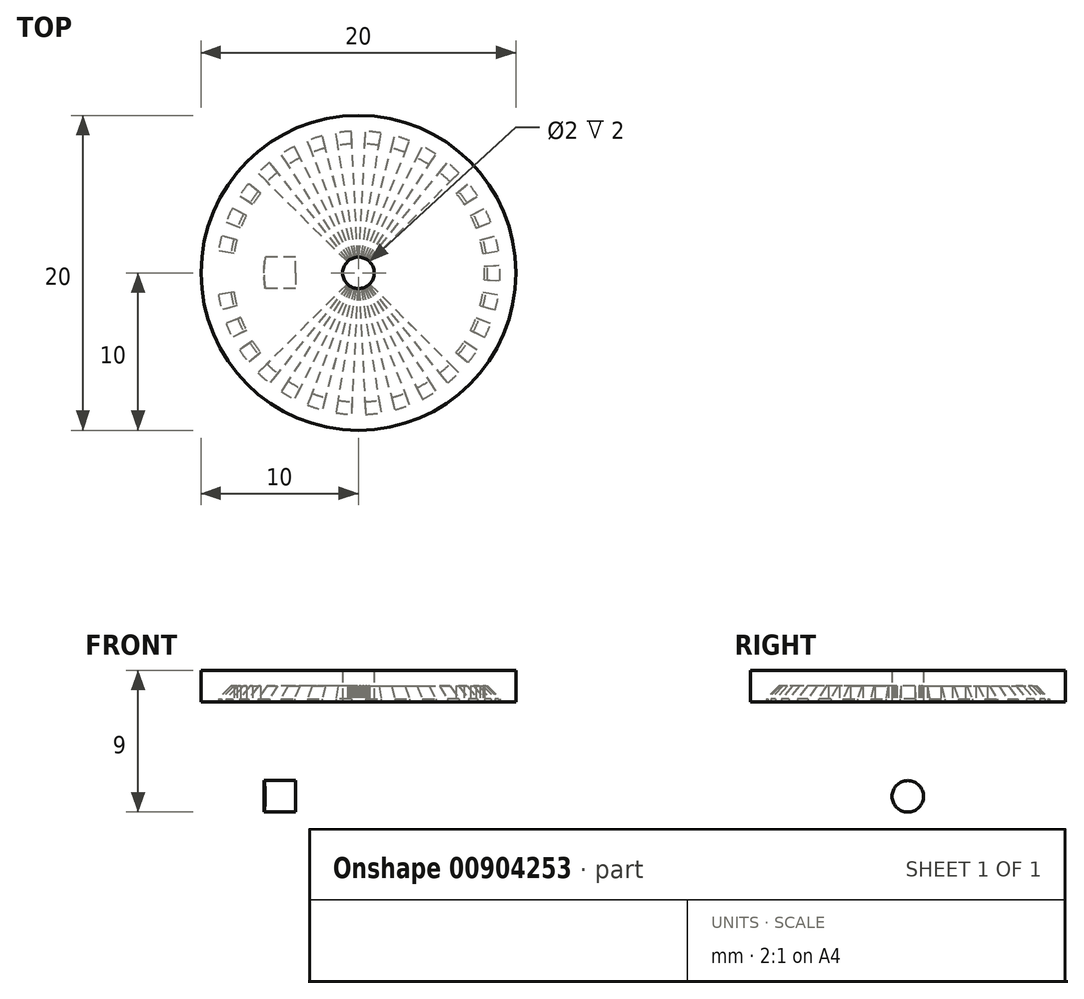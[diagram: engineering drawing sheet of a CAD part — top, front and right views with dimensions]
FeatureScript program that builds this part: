
annotation { "Feature Type Name" : "Feature", "Feature Type Description" : "" }
export const myFeature = defineFeature(function(context is Context, id is Id, definition is map)
    precondition{}
    {
        {
            var Q0;
            Q0=qCreatedBy(makeId("Front.planeOp"),FACE);
            var sketch = newSketch(context, id + "F0", { "sketchPlane" : qUnion([Q0])});
            skLineSegment(sketch, "E0.bottom", {"start": v(0, 0) * mm, "end": v(-5, 0) * mm});
            skLineSegment(sketch, "E0.top", {"start": v(0, 2) * mm, "end": v(-5, 2) * mm});
            skLineSegment(sketch, "E0.left", {"start": v(0, 0) * mm, "end": v(0, 2) * mm});
            skLineSegment(sketch, "E0.right", {"start": v(-5, 0) * mm, "end": v(-5, 2) * mm});
            skLineSegment(sketch, "E1.bottom", {"start": v(-5, 2) * mm, "end": v(-4, 2) * mm});
            skLineSegment(sketch, "E1.top", {"start": v(-5, 1) * mm, "end": v(-4, 1) * mm});
            skLineSegment(sketch, "E1.left", {"start": v(-5, 2) * mm, "end": v(-5, 1) * mm});
            skLineSegment(sketch, "E1.right", {"start": v(-4, 2) * mm, "end": v(-4, 1) * mm});
            skLineSegment(sketch, "E2.bottom", {"start": v(-4, 1) * mm, "end": v(-6, 1) * mm});
            skLineSegment(sketch, "E2.top", {"start": v(-4, 11) * mm, "end": v(-6, 11) * mm});
            skLineSegment(sketch, "E2.left", {"start": v(-4, 1) * mm, "end": v(-4, 11) * mm});
            skLineSegment(sketch, "E2.right", {"start": v(-6, 1) * mm, "end": v(-6, 11) * mm});
            skLineSegment(sketch, "E3", {"start": v(-1, 2) * mm, "end": v(-1, 0) * mm});
            skLineSegment(sketch, "E4.bottom", {"start": v(-6, 1) * mm, "end": v(-5, 1) * mm});
            skLineSegment(sketch, "E4.top", {"start": v(-6, 0) * mm, "end": v(-5, 0) * mm});
            skLineSegment(sketch, "E4.left", {"start": v(-6, 1) * mm, "end": v(-6, 0) * mm});
            skLineSegment(sketch, "E4.right", {"start": v(-5, 1) * mm, "end": v(-5, 0) * mm});
            skLineSegment(sketch, "E5.bottom", {"start": v(0, 0) * mm, "end": v(-6, 0) * mm});
            skLineSegment(sketch, "E5.top", {"start": v(0, -2) * mm, "end": v(-6, -2) * mm});
            skLineSegment(sketch, "E5.left", {"start": v(0, 0) * mm, "end": v(0, -2) * mm});
            skLineSegment(sketch, "E5.right", {"start": v(-6, 0) * mm, "end": v(-6, -2) * mm});
            skLineSegment(sketch, "E6.bottom", {"start": v(0, -2) * mm, "end": v(0, -2) * mm});
            skLineSegment(sketch, "E6.top", {"start": v(0, 0) * mm, "end": v(0, 0) * mm});
            skLineSegment(sketch, "E6.left", {"start": v(0, -2) * mm, "end": v(0, 0) * mm});
            skLineSegment(sketch, "E6.right", {"start": v(0, -2) * mm, "end": v(0, 0) * mm});
            skLineSegment(sketch, "E7.bottom", {"start": v(-6, -2) * mm, "end": v(-8, -2) * mm});
            skLineSegment(sketch, "E7.top", {"start": v(-6, 11) * mm, "end": v(-8, 11) * mm});
            skLineSegment(sketch, "E7.left", {"start": v(-6, -2) * mm, "end": v(-6, 11) * mm});
            skLineSegment(sketch, "E7.right", {"start": v(-8, -2) * mm, "end": v(-8, 11) * mm});
            skLineSegment(sketch, "E8.bottom", {"start": v(-4, 11) * mm, "end": v(-5, 11) * mm});
            skLineSegment(sketch, "E8.top", {"start": v(-4, 10) * mm, "end": v(-5, 10) * mm});
            skLineSegment(sketch, "E8.left", {"start": v(-4, 11) * mm, "end": v(-4, 10) * mm});
            skLineSegment(sketch, "E8.right", {"start": v(-5, 11) * mm, "end": v(-5, 10) * mm});
            skLineSegment(sketch, "E9.bottom", {"start": v(-5, 10) * mm, "end": v(0, 10) * mm});
            skLineSegment(sketch, "E9.top", {"start": v(-5, 12) * mm, "end": v(0, 12) * mm});
            skLineSegment(sketch, "E9.left", {"start": v(-5, 10) * mm, "end": v(-5, 12) * mm});
            skLineSegment(sketch, "E9.right", {"start": v(0, 10) * mm, "end": v(0, 12) * mm});
            skLineSegment(sketch, "E10.bottom", {"start": v(-8, 11) * mm, "end": v(-5, 11) * mm});
            skLineSegment(sketch, "E10.top", {"start": v(-8, 12) * mm, "end": v(-5, 12) * mm});
            skLineSegment(sketch, "E10.left", {"start": v(-8, 11) * mm, "end": v(-8, 12) * mm});
            skLineSegment(sketch, "E10.right", {"start": v(-5, 11) * mm, "end": v(-5, 12) * mm});
            skLineSegment(sketch, "E11", {"start": v(-6, 11) * mm, "end": v(-6, 12) * mm});
            skLineSegment(sketch, "E12.bottom", {"start": v(0, 12) * mm, "end": v(-8, 12) * mm});
            skLineSegment(sketch, "E12.top", {"start": v(0, 14) * mm, "end": v(-8, 14) * mm});
            skLineSegment(sketch, "E12.left", {"start": v(0, 12) * mm, "end": v(0, 14) * mm});
            skLineSegment(sketch, "E12.right", {"start": v(-8, 12) * mm, "end": v(-8, 14) * mm});
            skLineSegment(sketch, "E13", {"start": v(-1, 0) * mm, "end": v(-1, -2) * mm});
            skLineSegment(sketch, "E14", {"start": v(-1, -2) * mm, "end": v(-1, 14) * mm});
            skLineSegment(sketch, "E15.bottom", {"start": v(-8, 12) * mm, "end": v(-10, 12) * mm});
            skLineSegment(sketch, "E15.top", {"start": v(-8, 14) * mm, "end": v(-10, 14) * mm});
            skLineSegment(sketch, "E15.right", {"start": v(-10, 12) * mm, "end": v(-10, 14) * mm});
            skSolve(sketch);
        }
        {
            var Q0;
            {var subQ5=sQuery(id+"F0.wireOp",EDGE,"E7.bottom");Q0=makeQuery(id+"F0.imprint","IMPRINT",FACE,{"disambiguationData":[TD([[makeQuery(id+"F0.imprint","IMPRINT",EDGE,{"derivedFrom":subQ5}),-1.0]])]});}
            var Q1;
            {var subQ5=sQuery(id+"F0.wireOp",EDGE,"E5.bottom");var subQ7=makeQuery(id+"F0.imprint","INTERSECT",VERTEX,{"derivedFrom":[sQuery(id+"F0.wireOp",EDGE,"E4.right"),subQ5]});Q1=makeQuery(id+"F0.imprint","IMPRINT",FACE,{"disambiguationData":[TD([[makeQuery(id+"F0.imprint","IMPRINT",EDGE,{"disambiguationData":[TD([[subQ7,1.0]])],"derivedFrom":subQ5}),1.0]])]});}
            var Q2;
            {var subQ0=sQuery(id+"F0.wireOp",EDGE,"E12.right");Q2=makeQuery(id+"F0.imprint","IMPRINT",FACE,{"disambiguationData":[TD([[makeQuery(id+"F0.imprint","IMPRINT",EDGE,{"derivedFrom":subQ0}),-1.0]])]});}
            var Q3;
            Q3=makeQuery(id+"F0.imprint","IMPRINT",FACE,{"disambiguationData":[TD([[makeQuery(id+"F0.imprint","IMPRINT",EDGE,{"derivedFrom":sQuery(id+"F0.wireOp",EDGE,"E15.bottom")}),-1.0]])]});
            var Q4;
            {var subQ2=sQuery(id+"F0.wireOp",EDGE,"E10.left");Q4=makeQuery(id+"F0.imprint","IMPRINT",FACE,{"disambiguationData":[TD([[makeQuery(id+"F0.imprint","IMPRINT",EDGE,{"derivedFrom":subQ2}),-1.0]])]});}
            var Q5;
            Q5=sQuery(id+"F0.wireOp",EDGE,"E9.right");
            revolve(context, id + "F1", {"surfaceOperationType" : NewSurfaceOperationType.NEW, "entities" : qUnion([Q0, Q1, Q2, Q3, Q4]), "axis" : qUnion([Q5]), "revolveType" : RevolveType.FULL});
        }
        {
            var Q0;
            Q0=qCreatedBy(makeId("Front.planeOp"),FACE);
            var sketch = newSketch(context, id + "F2", { "sketchPlane" : qUnion([Q0])});
            skLineSegment(sketch, "E16.0", {"start": v(6, 0) * mm, "end": v(-6, 0) * mm});
            skLineSegment(sketch, "E17.0", {"start": v(10, 12) * mm, "end": v(-10, 12) * mm});
            skLineSegment(sketch, "E18", {"start": v(-6, 0) * mm, "end": v(-6, 12) * mm});
            skLineSegment(sketch, "E19", {"start": v(6, 0) * mm, "end": v(6, 12) * mm});
            skSolve(sketch);
        }
        {
            var Q0;
            Q0=makeQuery(id+"F2.imprint","IMPRINT",FACE,{"disambiguationData":[TD([[makeQuery(id+"F2.imprint","IMPRINT",EDGE,{"derivedFrom":sQuery(id+"F2.wireOp",EDGE,"E16.0")}),-1.0]])]});
            extrude(context, id + "F3", {"entities" : qUnion([Q0]), "operationType" : NewBodyOperationType.REMOVE, "oppositeDirection" : true, "depth" : 25 * mm, "offsetDistance" : 25 * mm});
        }
        {
            var Q0;
            Q0=makeQuery(id+"F2.imprint","IMPRINT",FACE,{"disambiguationData":[TD([[makeQuery(id+"F2.imprint","IMPRINT",EDGE,{"derivedFrom":sQuery(id+"F2.wireOp",EDGE,"E16.0")}),-1.0]])]});
            extrude(context, id + "F4", {"entities" : qUnion([Q0]), "operationType" : NewBodyOperationType.REMOVE, "oppositeDirection" : true, "depth" : -25 * mm, "offsetDistance" : 25 * mm});
        }
        {
            var Q0;
            Q0=makeQuery(id+"F1.opRevolve","SWEPT_FACE",FACE,{"disambiguationData":[OSD([sQuery(id+"F0.wireOp",EDGE,"E12.top"),sQuery(id+"F0.wireOp",EDGE,"E15.top")])]});
            var sketch = newSketch(context, id + "F5", { "sketchPlane" : qUnion([Q0])});
            skLineSegment(sketch, "E20", {"start": v(-0.5, 9.99) * mm, "end": v(0.5, 9.99) * mm});
            skLineSegment(sketch, "E21", {"start": v(0, 0) * mm, "end": v(0.5, 9.99) * mm});
            skLineSegment(sketch, "E22", {"start": v(0, 0) * mm, "end": v(-0.5, 9.99) * mm});
            skCircle(sketch, "E23", {"center": v(0, 0) * mm, "radius": 9 * mm});
            skLineSegment(sketch, "E24", {"start": v(0, 0) * mm, "end": v(9, 0) * mm});
            skLineSegment(sketch, "E25", {"start": v(9, 0) * mm, "end": v(10, 0) * mm});
            skLineSegment(sketch, "E26.1.0", {"start": v(0, 0) * mm, "end": v(-2.57, 9.67) * mm});
            skLineSegment(sketch, "E26.1.1", {"start": v(0, 0) * mm, "end": v(-1.59, 9.87) * mm});
            skLineSegment(sketch, "E26.2.0", {"start": v(0, 0) * mm, "end": v(-4.52, 8.92) * mm});
            skLineSegment(sketch, "E26.2.1", {"start": v(0, 0) * mm, "end": v(-3.6, 9.33) * mm});
            skLineSegment(sketch, "E27.2.3.0", {"start": v(0, 0) * mm, "end": v(-6.28, 7.79) * mm});
            skLineSegment(sketch, "E27.3.3.0", {"start": v(0, 0) * mm, "end": v(-5.47, 8.37) * mm});
            skLineSegment(sketch, "E27.2.4.0", {"start": v(0, 0) * mm, "end": v(-7.76, 6.31) * mm});
            skLineSegment(sketch, "E27.3.4.0", {"start": v(0, 0) * mm, "end": v(-7.09, 7.05) * mm});
            skLineSegment(sketch, "E27.2.5.0", {"start": v(0, 0) * mm, "end": v(-8.9, 4.56) * mm});
            skLineSegment(sketch, "E27.3.5.0", {"start": v(0, 0) * mm, "end": v(-8.4, 5.43) * mm});
            skLineSegment(sketch, "E27.2.6.0", {"start": v(0, 0) * mm, "end": v(-9.65, 2.61) * mm});
            skLineSegment(sketch, "E27.3.6.0", {"start": v(0, 0) * mm, "end": v(-9.34, 3.56) * mm});
            skLineSegment(sketch, "E27.2.7.0", {"start": v(0, 0) * mm, "end": v(-9.99, 0.55) * mm});
            skLineSegment(sketch, "E27.3.7.0", {"start": v(0, 0) * mm, "end": v(-9.88, 1.54) * mm});
            skLineSegment(sketch, "E27.2.8.0", {"start": v(0, 0) * mm, "end": v(-9.88, -1.54) * mm});
            skLineSegment(sketch, "E27.3.8.0", {"start": v(0, 0) * mm, "end": v(-9.99, -0.55) * mm});
            skLineSegment(sketch, "E27.2.9.0", {"start": v(0, 0) * mm, "end": v(-9.34, -3.56) * mm});
            skLineSegment(sketch, "E27.3.9.0", {"start": v(0, 0) * mm, "end": v(-9.65, -2.61) * mm});
            skLineSegment(sketch, "E27.2.10.0", {"start": v(0, 0) * mm, "end": v(-8.4, -5.43) * mm});
            skLineSegment(sketch, "E27.3.10.0", {"start": v(0, 0) * mm, "end": v(-8.9, -4.56) * mm});
            skLineSegment(sketch, "E27.2.11.0", {"start": v(0, 0) * mm, "end": v(-7.09, -7.05) * mm});
            skLineSegment(sketch, "E27.3.11.0", {"start": v(0, 0) * mm, "end": v(-7.76, -6.31) * mm});
            skLineSegment(sketch, "E27.2.12.0", {"start": v(0, 0) * mm, "end": v(-5.47, -8.37) * mm});
            skLineSegment(sketch, "E27.3.12.0", {"start": v(0, 0) * mm, "end": v(-6.28, -7.79) * mm});
            skLineSegment(sketch, "E27.2.13.0", {"start": v(0, 0) * mm, "end": v(-3.6, -9.33) * mm});
            skLineSegment(sketch, "E27.3.13.0", {"start": v(0, 0) * mm, "end": v(-4.52, -8.92) * mm});
            skLineSegment(sketch, "E27.2.14.0", {"start": v(0, 0) * mm, "end": v(-1.59, -9.87) * mm});
            skLineSegment(sketch, "E27.3.14.0", {"start": v(0, 0) * mm, "end": v(-2.57, -9.67) * mm});
            skLineSegment(sketch, "E27.2.15.0", {"start": v(0, 0) * mm, "end": v(0.5, -9.99) * mm});
            skLineSegment(sketch, "E27.3.15.0", {"start": v(0, 0) * mm, "end": v(-0.5, -9.99) * mm});
            skLineSegment(sketch, "E27.2.16.0", {"start": v(0, 0) * mm, "end": v(2.57, -9.67) * mm});
            skLineSegment(sketch, "E27.3.16.0", {"start": v(0, 0) * mm, "end": v(1.59, -9.87) * mm});
            skLineSegment(sketch, "E27.2.17.0", {"start": v(0, 0) * mm, "end": v(4.52, -8.92) * mm});
            skLineSegment(sketch, "E27.3.17.0", {"start": v(0, 0) * mm, "end": v(3.6, -9.33) * mm});
            skLineSegment(sketch, "E27.2.18.0", {"start": v(0, 0) * mm, "end": v(6.28, -7.79) * mm});
            skLineSegment(sketch, "E27.3.18.0", {"start": v(0, 0) * mm, "end": v(5.47, -8.37) * mm});
            skLineSegment(sketch, "E27.2.19.0", {"start": v(0, 0) * mm, "end": v(7.76, -6.31) * mm});
            skLineSegment(sketch, "E27.3.19.0", {"start": v(0, 0) * mm, "end": v(7.09, -7.05) * mm});
            skLineSegment(sketch, "E27.2.20.0", {"start": v(0, 0) * mm, "end": v(8.9, -4.56) * mm});
            skLineSegment(sketch, "E27.3.20.0", {"start": v(0, 0) * mm, "end": v(8.4, -5.43) * mm});
            skLineSegment(sketch, "E27.2.21.0", {"start": v(0, 0) * mm, "end": v(9.65, -2.61) * mm});
            skLineSegment(sketch, "E27.3.21.0", {"start": v(0, 0) * mm, "end": v(9.34, -3.56) * mm});
            skLineSegment(sketch, "E27.2.22.0", {"start": v(0, 0) * mm, "end": v(9.99, -0.55) * mm});
            skLineSegment(sketch, "E27.3.22.0", {"start": v(0, 0) * mm, "end": v(9.88, -1.54) * mm});
            skLineSegment(sketch, "E27.2.23.0", {"start": v(0, 0) * mm, "end": v(9.88, 1.54) * mm});
            skLineSegment(sketch, "E27.3.23.0", {"start": v(0, 0) * mm, "end": v(9.99, 0.55) * mm});
            skLineSegment(sketch, "E27.2.24.0", {"start": v(0, 0) * mm, "end": v(9.34, 3.56) * mm});
            skLineSegment(sketch, "E27.3.24.0", {"start": v(0, 0) * mm, "end": v(9.65, 2.61) * mm});
            skLineSegment(sketch, "E28.2.25.0", {"start": v(0, 0) * mm, "end": v(8.4, 5.43) * mm});
            skLineSegment(sketch, "E28.3.25.0", {"start": v(0, 0) * mm, "end": v(8.9, 4.56) * mm});
            skLineSegment(sketch, "E29.2.26.0", {"start": v(0, 0) * mm, "end": v(7.09, 7.05) * mm});
            skLineSegment(sketch, "E29.3.26.0", {"start": v(0, 0) * mm, "end": v(7.76, 6.31) * mm});
            skLineSegment(sketch, "E29.2.27.0", {"start": v(0, 0) * mm, "end": v(5.47, 8.37) * mm});
            skLineSegment(sketch, "E29.3.27.0", {"start": v(0, 0) * mm, "end": v(6.28, 7.79) * mm});
            skLineSegment(sketch, "E29.2.28.0", {"start": v(0, 0) * mm, "end": v(3.6, 9.33) * mm});
            skLineSegment(sketch, "E29.3.28.0", {"start": v(0, 0) * mm, "end": v(4.52, 8.92) * mm});
            skLineSegment(sketch, "E29.2.29.0", {"start": v(0, 0) * mm, "end": v(1.59, 9.87) * mm});
            skLineSegment(sketch, "E29.3.29.0", {"start": v(0, 0) * mm, "end": v(2.57, 9.67) * mm});
            skSolve(sketch);
        }
        {
            var Q0;
            {var subQ0=sQuery(id+"F2.wireOp",EDGE,"E18");Q0=makeQuery(id+"F4.boolean.opBoolean","MERGE",FACE,{"derivedFrom":[makeQuery(id+"F3.boolean.opBoolean","COPY",FACE,{"derivedFrom":makeQuery(id+"F3.opExtrude","SWEPT_FACE",FACE,{"disambiguationData":[OSD([subQ0])]})})],"fromTools":[makeQuery(id+"F4.opExtrude","SWEPT_FACE",FACE,{"disambiguationData":[OSD([subQ0])]})]});}
            var sketch = newSketch(context, id + "F6", { "sketchPlane" : qUnion([Q0])});
            skLineSegment(sketch, "E30.0", {"start": v(10, 12) * mm, "end": v(-10, 12) * mm});
            skLineSegment(sketch, "E31.0", {"start": v(5.3, 0) * mm, "end": v(8, 0) * mm});
            skLineSegment(sketch, "E32.0", {"start": v(-5.3, 0) * mm, "end": v(-8, 0) * mm});
            skLineSegment(sketch, "E33", {"start": v(-5.3, 0) * mm, "end": v(5.3, 0) * mm});
            skLineSegment(sketch, "E34", {"start": v(0, 0) * mm, "end": v(0, 12) * mm});
            skLineSegment(sketch, "E35.0", {"start": v(-5.3, 12) * mm, "end": v(-5.3, 0) * mm});
            skLineSegment(sketch, "E36.0", {"start": v(5.3, 12) * mm, "end": v(5.3, 0) * mm});
            skLineSegment(sketch, "E37", {"start": v(-5.3, 6) * mm, "end": v(5.3, 6) * mm});
            skCircle(sketch, "E38", {"center": v(0, 6) * mm, "radius": 1 * mm});
            skSolve(sketch);
        }
        {
            var Q0;
            {var subQ0=sQuery(id+"F6.wireOp",EDGE,"E37");var subQ1=sQuery(id+"F6.wireOp",EDGE,"E34");var subQ2=makeQuery(id+"F6.imprint","INTERSECT",VERTEX,{"derivedFrom":[subQ1,subQ0]});Q0=makeQuery(id+"F6.imprint","IMPRINT",FACE,{"disambiguationData":[TD([[makeQuery(id+"F6.imprint","IMPRINT",EDGE,{"disambiguationData":[TD([[subQ2,-1.0]])],"derivedFrom":subQ1}),-1.0]])]});}
            var Q1;
            {var subQ0=sQuery(id+"F6.wireOp",EDGE,"E38");var subQ1=sQuery(id+"F6.wireOp",EDGE,"E34");var subQ2=makeQuery(id+"F6.imprint","INTERSECT",VERTEX,{"disambiguationData":[OD(0.0)],"derivedFrom":[subQ1,subQ0]});Q1=makeQuery(id+"F6.imprint","IMPRINT",FACE,{"disambiguationData":[TD([[makeQuery(id+"F6.imprint","IMPRINT",EDGE,{"disambiguationData":[TD([[subQ2,-1.0]])],"derivedFrom":subQ1}),-1.0]])]});}
            var Q2;
            {var subQ0=sQuery(id+"F6.wireOp",EDGE,"E38");var subQ1=sQuery(id+"F6.wireOp",EDGE,"E34");var subQ2=makeQuery(id+"F6.imprint","INTERSECT",VERTEX,{"disambiguationData":[OD(0.0)],"derivedFrom":[subQ1,subQ0]});Q2=makeQuery(id+"F6.imprint","IMPRINT",FACE,{"disambiguationData":[TD([[makeQuery(id+"F6.imprint","IMPRINT",EDGE,{"disambiguationData":[TD([[subQ2,-1.0]])],"derivedFrom":subQ1}),1.0]])]});}
            var Q3;
            {var subQ0=sQuery(id+"F6.wireOp",EDGE,"E37");var subQ1=sQuery(id+"F6.wireOp",EDGE,"E34");var subQ2=makeQuery(id+"F6.imprint","INTERSECT",VERTEX,{"derivedFrom":[subQ1,subQ0]});Q3=makeQuery(id+"F6.imprint","IMPRINT",FACE,{"disambiguationData":[TD([[makeQuery(id+"F6.imprint","IMPRINT",EDGE,{"disambiguationData":[TD([[subQ2,-1.0]])],"derivedFrom":subQ1}),1.0]])]});}
            extrude(context, id + "F7", {"entities" : qUnion([Q0, Q1, Q2, Q3]), "operationType" : NewBodyOperationType.ADD, "depth" : 2 * mm, "offsetDistance" : 25 * mm});
        }
        {
            var Q0;
            {var subQ0=sQuery(id+"F2.wireOp",EDGE,"E17.0");Q0=makeQuery(id+"F4.boolean.opBoolean","MERGE",FACE,{"derivedFrom":[makeQuery(id+"F3.boolean.opBoolean","MERGE",FACE,{"derivedFrom":[makeQuery(id+"F1.opRevolve","SWEPT_FACE",FACE,{"disambiguationData":[OSD([sQuery(id+"F0.wireOp",EDGE,"E12.bottom")])]}),makeQuery(id+"F1.opRevolve","SWEPT_FACE",FACE,{"disambiguationData":[OSD([sQuery(id+"F0.wireOp",EDGE,"E15.bottom")])]})],"fromTools":[makeQuery(id+"F3.opExtrude","SWEPT_FACE",FACE,{"disambiguationData":[OSD([subQ0])]})]})],"fromTools":[makeQuery(id+"F4.opExtrude","SWEPT_FACE",FACE,{"disambiguationData":[OSD([subQ0])]})]});}
            var sketch = newSketch(context, id + "F8", { "sketchPlane" : qUnion([Q0])});
            skCircle(sketch, "E39.0", {"center": v(0, 0) * mm, "radius": 9 * mm});
            skLineSegment(sketch, "E40.0", {"start": v(0, 0) * mm, "end": v(-7.76, 6.31) * mm});
            skLineSegment(sketch, "E41.0", {"start": v(0, 0) * mm, "end": v(-7.09, 7.05) * mm});
            skLineSegment(sketch, "E42.0", {"start": v(0, 0) * mm, "end": v(-6.28, 7.79) * mm});
            skLineSegment(sketch, "E43.0", {"start": v(0, 0) * mm, "end": v(-5.47, 8.37) * mm});
            skLineSegment(sketch, "E44.0", {"start": v(0, 0) * mm, "end": v(-4.52, 8.92) * mm});
            skLineSegment(sketch, "E45.0", {"start": v(0, 0) * mm, "end": v(-3.6, 9.33) * mm});
            skLineSegment(sketch, "E46.0", {"start": v(0, 0) * mm, "end": v(-2.57, 9.67) * mm});
            skLineSegment(sketch, "E47.0", {"start": v(0, 0) * mm, "end": v(-1.59, 9.87) * mm});
            skLineSegment(sketch, "E48.0", {"start": v(0, 0) * mm, "end": v(-0.5, 9.99) * mm});
            skLineSegment(sketch, "E49.0", {"start": v(0, 0) * mm, "end": v(0.5, 9.99) * mm});
            skLineSegment(sketch, "E50.0", {"start": v(0, 0) * mm, "end": v(1.59, 9.87) * mm});
            skLineSegment(sketch, "E51.0", {"start": v(0, 0) * mm, "end": v(2.57, 9.67) * mm});
            skLineSegment(sketch, "E52.0", {"start": v(0, 0) * mm, "end": v(3.6, 9.33) * mm});
            skLineSegment(sketch, "E53.0", {"start": v(0, 0) * mm, "end": v(4.52, 8.92) * mm});
            skLineSegment(sketch, "E54.0", {"start": v(0, 0) * mm, "end": v(5.47, 8.37) * mm});
            skLineSegment(sketch, "E55.0", {"start": v(0, 0) * mm, "end": v(6.28, 7.79) * mm});
            skLineSegment(sketch, "E56.0", {"start": v(0, 0) * mm, "end": v(7.09, 7.05) * mm});
            skLineSegment(sketch, "E57.0", {"start": v(0, 0) * mm, "end": v(7.76, 6.31) * mm});
            skLineSegment(sketch, "E58.0", {"start": v(0, 0) * mm, "end": v(8.4, 5.43) * mm});
            skLineSegment(sketch, "E59.0", {"start": v(0, 0) * mm, "end": v(8.9, 4.56) * mm});
            skLineSegment(sketch, "E60.0", {"start": v(0, 0) * mm, "end": v(9.34, 3.56) * mm});
            skLineSegment(sketch, "E61.0", {"start": v(0, 0) * mm, "end": v(9.65, 2.61) * mm});
            skLineSegment(sketch, "E62.0", {"start": v(0, 0) * mm, "end": v(9.88, 1.54) * mm});
            skLineSegment(sketch, "E63.0", {"start": v(0, 0) * mm, "end": v(9.99, 0.55) * mm});
            skLineSegment(sketch, "E64.0", {"start": v(0, 0) * mm, "end": v(9.99, -0.55) * mm});
            skLineSegment(sketch, "E65.0", {"start": v(0, 0) * mm, "end": v(9.88, -1.54) * mm});
            skLineSegment(sketch, "E66.0", {"start": v(0, 0) * mm, "end": v(9.65, -2.61) * mm});
            skLineSegment(sketch, "E67.0", {"start": v(0, 0) * mm, "end": v(9.34, -3.56) * mm});
            skLineSegment(sketch, "E68.0", {"start": v(0, 0) * mm, "end": v(8.9, -4.56) * mm});
            skLineSegment(sketch, "E69.0", {"start": v(0, 0) * mm, "end": v(8.4, -5.43) * mm});
            skLineSegment(sketch, "E70.0", {"start": v(0, 0) * mm, "end": v(7.76, -6.31) * mm});
            skLineSegment(sketch, "E71.0", {"start": v(0, 0) * mm, "end": v(7.09, -7.05) * mm});
            skLineSegment(sketch, "E72.0", {"start": v(0, 0) * mm, "end": v(6.28, -7.79) * mm});
            skLineSegment(sketch, "E73.0", {"start": v(0, 0) * mm, "end": v(5.47, -8.37) * mm});
            skLineSegment(sketch, "E74.0", {"start": v(0, 0) * mm, "end": v(4.52, -8.92) * mm});
            skLineSegment(sketch, "E75.0", {"start": v(0, 0) * mm, "end": v(3.6, -9.33) * mm});
            skLineSegment(sketch, "E76.0", {"start": v(0, 0) * mm, "end": v(2.57, -9.67) * mm});
            skLineSegment(sketch, "E77.0", {"start": v(0, 0) * mm, "end": v(1.59, -9.87) * mm});
            skLineSegment(sketch, "E78.0", {"start": v(0, 0) * mm, "end": v(0.5, -9.99) * mm});
            skLineSegment(sketch, "E79.0", {"start": v(0, 0) * mm, "end": v(-0.5, -9.99) * mm});
            skLineSegment(sketch, "E80.0", {"start": v(0, 0) * mm, "end": v(-1.59, -9.87) * mm});
            skLineSegment(sketch, "E81.0", {"start": v(0, 0) * mm, "end": v(-2.57, -9.67) * mm});
            skLineSegment(sketch, "E82.0", {"start": v(0, 0) * mm, "end": v(-3.6, -9.33) * mm});
            skLineSegment(sketch, "E83.0", {"start": v(0, 0) * mm, "end": v(-4.52, -8.92) * mm});
            skLineSegment(sketch, "E84.0", {"start": v(0, 0) * mm, "end": v(-5.47, -8.37) * mm});
            skLineSegment(sketch, "E85.0", {"start": v(0, 0) * mm, "end": v(-6.28, -7.79) * mm});
            skLineSegment(sketch, "E86.0", {"start": v(0, 0) * mm, "end": v(-7.09, -7.05) * mm});
            skLineSegment(sketch, "E87.0", {"start": v(0, 0) * mm, "end": v(-7.76, -6.31) * mm});
            skLineSegment(sketch, "E88.0", {"start": v(0, 0) * mm, "end": v(-8.4, -5.43) * mm});
            skLineSegment(sketch, "E89.0", {"start": v(0, 0) * mm, "end": v(-8.9, -4.56) * mm});
            skLineSegment(sketch, "E90.0", {"start": v(0, 0) * mm, "end": v(-9.34, -3.56) * mm});
            skLineSegment(sketch, "E91.0", {"start": v(0, 0) * mm, "end": v(-9.65, -2.61) * mm});
            skLineSegment(sketch, "E92.0", {"start": v(0, 0) * mm, "end": v(-9.88, -1.54) * mm});
            skLineSegment(sketch, "E93.0", {"start": v(0, 0) * mm, "end": v(-9.99, -0.55) * mm});
            skLineSegment(sketch, "E94.0", {"start": v(0, 0) * mm, "end": v(-9.99, 0.55) * mm});
            skLineSegment(sketch, "E95.0", {"start": v(0, 0) * mm, "end": v(-9.88, 1.54) * mm});
            skLineSegment(sketch, "E96.0", {"start": v(0, 0) * mm, "end": v(-9.65, 2.61) * mm});
            skLineSegment(sketch, "E97.0", {"start": v(0, 0) * mm, "end": v(-9.34, 3.56) * mm});
            skLineSegment(sketch, "E98.0", {"start": v(0, 0) * mm, "end": v(-8.9, 4.56) * mm});
            skLineSegment(sketch, "E99.0", {"start": v(0, 0) * mm, "end": v(-8.4, 5.43) * mm});
            skSolve(sketch);
        }
        {
            var Q0;
            {var subQ0=sQuery(id+"F8.wireOp",EDGE,"E48.0");var subQ1=sQuery(id+"F8.wireOp",EDGE,"E39.0");var subQ2=makeQuery(id+"F8.imprint","INTERSECT",VERTEX,{"derivedFrom":[subQ1,subQ0]});Q0=makeQuery(id+"F8.imprint","IMPRINT",FACE,{"disambiguationData":[TD([[makeQuery(id+"F8.imprint","IMPRINT",EDGE,{"disambiguationData":[TD([[subQ2,-1.0]])],"derivedFrom":subQ1}),1.0]])]});}
            var Q1;
            {var subQ0=sQuery(id+"F8.wireOp",EDGE,"E50.0");var subQ1=sQuery(id+"F8.wireOp",EDGE,"E39.0");var subQ2=makeQuery(id+"F8.imprint","INTERSECT",VERTEX,{"derivedFrom":[subQ1,subQ0]});Q1=makeQuery(id+"F8.imprint","IMPRINT",FACE,{"disambiguationData":[TD([[makeQuery(id+"F8.imprint","IMPRINT",EDGE,{"disambiguationData":[TD([[subQ2,-1.0]])],"derivedFrom":subQ1}),1.0]])]});}
            var Q2;
            {var subQ0=sQuery(id+"F8.wireOp",EDGE,"E52.0");var subQ1=sQuery(id+"F8.wireOp",EDGE,"E39.0");var subQ2=makeQuery(id+"F8.imprint","INTERSECT",VERTEX,{"derivedFrom":[subQ1,subQ0]});Q2=makeQuery(id+"F8.imprint","IMPRINT",FACE,{"disambiguationData":[TD([[makeQuery(id+"F8.imprint","IMPRINT",EDGE,{"disambiguationData":[TD([[subQ2,-1.0]])],"derivedFrom":subQ1}),1.0]])]});}
            var Q3;
            {var subQ0=sQuery(id+"F8.wireOp",EDGE,"E54.0");var subQ1=sQuery(id+"F8.wireOp",EDGE,"E39.0");var subQ2=makeQuery(id+"F8.imprint","INTERSECT",VERTEX,{"derivedFrom":[subQ1,subQ0]});Q3=makeQuery(id+"F8.imprint","IMPRINT",FACE,{"disambiguationData":[TD([[makeQuery(id+"F8.imprint","IMPRINT",EDGE,{"disambiguationData":[TD([[subQ2,-1.0]])],"derivedFrom":subQ1}),1.0]])]});}
            var Q4;
            {var subQ0=sQuery(id+"F8.wireOp",EDGE,"E56.0");var subQ1=sQuery(id+"F8.wireOp",EDGE,"E39.0");var subQ2=makeQuery(id+"F8.imprint","INTERSECT",VERTEX,{"derivedFrom":[subQ1,subQ0]});Q4=makeQuery(id+"F8.imprint","IMPRINT",FACE,{"disambiguationData":[TD([[makeQuery(id+"F8.imprint","IMPRINT",EDGE,{"disambiguationData":[TD([[subQ2,-1.0]])],"derivedFrom":subQ1}),1.0]])]});}
            var Q5;
            {var subQ0=sQuery(id+"F8.wireOp",EDGE,"E58.0");var subQ1=sQuery(id+"F8.wireOp",EDGE,"E39.0");var subQ2=makeQuery(id+"F8.imprint","INTERSECT",VERTEX,{"derivedFrom":[subQ1,subQ0]});Q5=makeQuery(id+"F8.imprint","IMPRINT",FACE,{"disambiguationData":[TD([[makeQuery(id+"F8.imprint","IMPRINT",EDGE,{"disambiguationData":[TD([[subQ2,-1.0]])],"derivedFrom":subQ1}),1.0]])]});}
            var Q6;
            {var subQ0=sQuery(id+"F8.wireOp",EDGE,"E60.0");var subQ1=sQuery(id+"F8.wireOp",EDGE,"E39.0");var subQ2=makeQuery(id+"F8.imprint","INTERSECT",VERTEX,{"derivedFrom":[subQ1,subQ0]});Q6=makeQuery(id+"F8.imprint","IMPRINT",FACE,{"disambiguationData":[TD([[makeQuery(id+"F8.imprint","IMPRINT",EDGE,{"disambiguationData":[TD([[subQ2,-1.0]])],"derivedFrom":subQ1}),1.0]])]});}
            var Q7;
            {var subQ0=sQuery(id+"F8.wireOp",EDGE,"E62.0");var subQ1=sQuery(id+"F8.wireOp",EDGE,"E39.0");var subQ2=makeQuery(id+"F8.imprint","INTERSECT",VERTEX,{"derivedFrom":[subQ1,subQ0]});Q7=makeQuery(id+"F8.imprint","IMPRINT",FACE,{"disambiguationData":[TD([[makeQuery(id+"F8.imprint","IMPRINT",EDGE,{"disambiguationData":[TD([[subQ2,-1.0]])],"derivedFrom":subQ1}),1.0]])]});}
            var Q8;
            {var subQ0=sQuery(id+"F8.wireOp",EDGE,"E64.0");var subQ1=sQuery(id+"F8.wireOp",EDGE,"E39.0");var subQ2=makeQuery(id+"F8.imprint","INTERSECT",VERTEX,{"derivedFrom":[subQ1,subQ0]});Q8=makeQuery(id+"F8.imprint","IMPRINT",FACE,{"disambiguationData":[TD([[makeQuery(id+"F8.imprint","IMPRINT",EDGE,{"disambiguationData":[TD([[subQ2,-1.0]])],"derivedFrom":subQ1}),1.0]])]});}
            var Q9;
            {var subQ0=sQuery(id+"F8.wireOp",EDGE,"E66.0");var subQ1=sQuery(id+"F8.wireOp",EDGE,"E39.0");var subQ2=makeQuery(id+"F8.imprint","INTERSECT",VERTEX,{"derivedFrom":[subQ1,subQ0]});Q9=makeQuery(id+"F8.imprint","IMPRINT",FACE,{"disambiguationData":[TD([[makeQuery(id+"F8.imprint","IMPRINT",EDGE,{"disambiguationData":[TD([[subQ2,-1.0]])],"derivedFrom":subQ1}),1.0]])]});}
            var Q10;
            {var subQ0=sQuery(id+"F8.wireOp",EDGE,"E68.0");var subQ1=sQuery(id+"F8.wireOp",EDGE,"E39.0");var subQ2=makeQuery(id+"F8.imprint","INTERSECT",VERTEX,{"derivedFrom":[subQ1,subQ0]});Q10=makeQuery(id+"F8.imprint","IMPRINT",FACE,{"disambiguationData":[TD([[makeQuery(id+"F8.imprint","IMPRINT",EDGE,{"disambiguationData":[TD([[subQ2,-1.0]])],"derivedFrom":subQ1}),1.0]])]});}
            var Q11;
            {var subQ0=sQuery(id+"F8.wireOp",EDGE,"E70.0");var subQ1=sQuery(id+"F8.wireOp",EDGE,"E39.0");var subQ2=makeQuery(id+"F8.imprint","INTERSECT",VERTEX,{"derivedFrom":[subQ1,subQ0]});Q11=makeQuery(id+"F8.imprint","IMPRINT",FACE,{"disambiguationData":[TD([[makeQuery(id+"F8.imprint","IMPRINT",EDGE,{"disambiguationData":[TD([[subQ2,-1.0]])],"derivedFrom":subQ1}),1.0]])]});}
            var Q12;
            {var subQ0=sQuery(id+"F8.wireOp",EDGE,"E72.0");var subQ1=sQuery(id+"F8.wireOp",EDGE,"E39.0");var subQ2=makeQuery(id+"F8.imprint","INTERSECT",VERTEX,{"derivedFrom":[subQ1,subQ0]});Q12=makeQuery(id+"F8.imprint","IMPRINT",FACE,{"disambiguationData":[TD([[makeQuery(id+"F8.imprint","IMPRINT",EDGE,{"disambiguationData":[TD([[subQ2,-1.0]])],"derivedFrom":subQ1}),1.0]])]});}
            var Q13;
            {var subQ0=sQuery(id+"F8.wireOp",EDGE,"E46.0");var subQ1=sQuery(id+"F8.wireOp",EDGE,"E39.0");var subQ2=makeQuery(id+"F8.imprint","INTERSECT",VERTEX,{"derivedFrom":[subQ1,subQ0]});Q13=makeQuery(id+"F8.imprint","IMPRINT",FACE,{"disambiguationData":[TD([[makeQuery(id+"F8.imprint","IMPRINT",EDGE,{"disambiguationData":[TD([[subQ2,-1.0]])],"derivedFrom":subQ1}),1.0]])]});}
            var Q14;
            {var subQ0=sQuery(id+"F8.wireOp",EDGE,"E44.0");var subQ1=sQuery(id+"F8.wireOp",EDGE,"E39.0");var subQ2=makeQuery(id+"F8.imprint","INTERSECT",VERTEX,{"derivedFrom":[subQ1,subQ0]});Q14=makeQuery(id+"F8.imprint","IMPRINT",FACE,{"disambiguationData":[TD([[makeQuery(id+"F8.imprint","IMPRINT",EDGE,{"disambiguationData":[TD([[subQ2,-1.0]])],"derivedFrom":subQ1}),1.0]])]});}
            var Q15;
            {var subQ0=sQuery(id+"F8.wireOp",EDGE,"E42.0");var subQ1=sQuery(id+"F8.wireOp",EDGE,"E39.0");var subQ2=makeQuery(id+"F8.imprint","INTERSECT",VERTEX,{"derivedFrom":[subQ1,subQ0]});Q15=makeQuery(id+"F8.imprint","IMPRINT",FACE,{"disambiguationData":[TD([[makeQuery(id+"F8.imprint","IMPRINT",EDGE,{"disambiguationData":[TD([[subQ2,-1.0]])],"derivedFrom":subQ1}),1.0]])]});}
            var Q16;
            {var subQ0=sQuery(id+"F8.wireOp",EDGE,"E40.0");var subQ1=sQuery(id+"F8.wireOp",EDGE,"E39.0");var subQ2=makeQuery(id+"F8.imprint","INTERSECT",VERTEX,{"derivedFrom":[subQ1,subQ0]});Q16=makeQuery(id+"F8.imprint","IMPRINT",FACE,{"disambiguationData":[TD([[makeQuery(id+"F8.imprint","IMPRINT",EDGE,{"disambiguationData":[TD([[subQ2,-1.0]])],"derivedFrom":subQ1}),1.0]])]});}
            var Q17;
            {var subQ0=sQuery(id+"F8.wireOp",EDGE,"E98.0");var subQ1=sQuery(id+"F8.wireOp",EDGE,"E39.0");var subQ2=makeQuery(id+"F8.imprint","INTERSECT",VERTEX,{"derivedFrom":[subQ1,subQ0]});Q17=makeQuery(id+"F8.imprint","IMPRINT",FACE,{"disambiguationData":[TD([[makeQuery(id+"F8.imprint","IMPRINT",EDGE,{"disambiguationData":[TD([[subQ2,-1.0]])],"derivedFrom":subQ1}),1.0]])]});}
            var Q18;
            {var subQ0=sQuery(id+"F8.wireOp",EDGE,"E96.0");var subQ1=sQuery(id+"F8.wireOp",EDGE,"E39.0");var subQ2=makeQuery(id+"F8.imprint","INTERSECT",VERTEX,{"derivedFrom":[subQ1,subQ0]});Q18=makeQuery(id+"F8.imprint","IMPRINT",FACE,{"disambiguationData":[TD([[makeQuery(id+"F8.imprint","IMPRINT",EDGE,{"disambiguationData":[TD([[subQ2,-1.0]])],"derivedFrom":subQ1}),1.0]])]});}
            var Q19;
            {var subQ0=sQuery(id+"F8.wireOp",EDGE,"E95.0");var subQ1=sQuery(id+"F8.wireOp",EDGE,"E39.0");var subQ2=makeQuery(id+"F8.imprint","INTERSECT",VERTEX,{"derivedFrom":[subQ1,subQ0]});Q19=makeQuery(id+"F8.imprint","IMPRINT",FACE,{"disambiguationData":[TD([[makeQuery(id+"F8.imprint","IMPRINT",EDGE,{"disambiguationData":[TD([[subQ2,1.0]])],"derivedFrom":subQ1}),1.0]])]});}
            var Q20;
            {var subQ0=sQuery(id+"F8.wireOp",EDGE,"E92.0");var subQ1=sQuery(id+"F8.wireOp",EDGE,"E39.0");var subQ2=makeQuery(id+"F8.imprint","INTERSECT",VERTEX,{"derivedFrom":[subQ1,subQ0]});Q20=makeQuery(id+"F8.imprint","IMPRINT",FACE,{"disambiguationData":[TD([[makeQuery(id+"F8.imprint","IMPRINT",EDGE,{"disambiguationData":[TD([[subQ2,-1.0]])],"derivedFrom":subQ1}),1.0]])]});}
            var Q21;
            {var subQ0=sQuery(id+"F8.wireOp",EDGE,"E90.0");var subQ1=sQuery(id+"F8.wireOp",EDGE,"E39.0");var subQ2=makeQuery(id+"F8.imprint","INTERSECT",VERTEX,{"derivedFrom":[subQ1,subQ0]});Q21=makeQuery(id+"F8.imprint","IMPRINT",FACE,{"disambiguationData":[TD([[makeQuery(id+"F8.imprint","IMPRINT",EDGE,{"disambiguationData":[TD([[subQ2,-1.0]])],"derivedFrom":subQ1}),1.0]])]});}
            var Q22;
            {var subQ0=sQuery(id+"F8.wireOp",EDGE,"E88.0");var subQ1=sQuery(id+"F8.wireOp",EDGE,"E39.0");var subQ2=makeQuery(id+"F8.imprint","INTERSECT",VERTEX,{"derivedFrom":[subQ1,subQ0]});Q22=makeQuery(id+"F8.imprint","IMPRINT",FACE,{"disambiguationData":[TD([[makeQuery(id+"F8.imprint","IMPRINT",EDGE,{"disambiguationData":[TD([[subQ2,-1.0]])],"derivedFrom":subQ1}),1.0]])]});}
            var Q23;
            {var subQ0=sQuery(id+"F8.wireOp",EDGE,"E86.0");var subQ1=sQuery(id+"F8.wireOp",EDGE,"E39.0");var subQ2=makeQuery(id+"F8.imprint","INTERSECT",VERTEX,{"derivedFrom":[subQ1,subQ0]});Q23=makeQuery(id+"F8.imprint","IMPRINT",FACE,{"disambiguationData":[TD([[makeQuery(id+"F8.imprint","IMPRINT",EDGE,{"disambiguationData":[TD([[subQ2,-1.0]])],"derivedFrom":subQ1}),1.0]])]});}
            var Q24;
            {var subQ0=sQuery(id+"F8.wireOp",EDGE,"E74.0");var subQ1=sQuery(id+"F8.wireOp",EDGE,"E39.0");var subQ2=makeQuery(id+"F8.imprint","INTERSECT",VERTEX,{"derivedFrom":[subQ1,subQ0]});Q24=makeQuery(id+"F8.imprint","IMPRINT",FACE,{"disambiguationData":[TD([[makeQuery(id+"F8.imprint","IMPRINT",EDGE,{"disambiguationData":[TD([[subQ2,-1.0]])],"derivedFrom":subQ1}),1.0]])]});}
            var Q25;
            {var subQ0=sQuery(id+"F8.wireOp",EDGE,"E76.0");var subQ1=sQuery(id+"F8.wireOp",EDGE,"E39.0");var subQ2=makeQuery(id+"F8.imprint","INTERSECT",VERTEX,{"derivedFrom":[subQ1,subQ0]});Q25=makeQuery(id+"F8.imprint","IMPRINT",FACE,{"disambiguationData":[TD([[makeQuery(id+"F8.imprint","IMPRINT",EDGE,{"disambiguationData":[TD([[subQ2,-1.0]])],"derivedFrom":subQ1}),1.0]])]});}
            var Q26;
            {var subQ0=sQuery(id+"F8.wireOp",EDGE,"E78.0");var subQ1=sQuery(id+"F8.wireOp",EDGE,"E39.0");var subQ2=makeQuery(id+"F8.imprint","INTERSECT",VERTEX,{"derivedFrom":[subQ1,subQ0]});Q26=makeQuery(id+"F8.imprint","IMPRINT",FACE,{"disambiguationData":[TD([[makeQuery(id+"F8.imprint","IMPRINT",EDGE,{"disambiguationData":[TD([[subQ2,-1.0]])],"derivedFrom":subQ1}),1.0]])]});}
            var Q27;
            {var subQ0=sQuery(id+"F8.wireOp",EDGE,"E80.0");var subQ1=sQuery(id+"F8.wireOp",EDGE,"E39.0");var subQ2=makeQuery(id+"F8.imprint","INTERSECT",VERTEX,{"derivedFrom":[subQ1,subQ0]});Q27=makeQuery(id+"F8.imprint","IMPRINT",FACE,{"disambiguationData":[TD([[makeQuery(id+"F8.imprint","IMPRINT",EDGE,{"disambiguationData":[TD([[subQ2,-1.0]])],"derivedFrom":subQ1}),1.0]])]});}
            var Q28;
            {var subQ0=sQuery(id+"F8.wireOp",EDGE,"E82.0");var subQ1=sQuery(id+"F8.wireOp",EDGE,"E39.0");var subQ2=makeQuery(id+"F8.imprint","INTERSECT",VERTEX,{"derivedFrom":[subQ1,subQ0]});Q28=makeQuery(id+"F8.imprint","IMPRINT",FACE,{"disambiguationData":[TD([[makeQuery(id+"F8.imprint","IMPRINT",EDGE,{"disambiguationData":[TD([[subQ2,-1.0]])],"derivedFrom":subQ1}),1.0]])]});}
            var Q29;
            {var subQ0=sQuery(id+"F8.wireOp",EDGE,"E84.0");var subQ1=sQuery(id+"F8.wireOp",EDGE,"E39.0");var subQ2=makeQuery(id+"F8.imprint","INTERSECT",VERTEX,{"derivedFrom":[subQ1,subQ0]});Q29=makeQuery(id+"F8.imprint","IMPRINT",FACE,{"disambiguationData":[TD([[makeQuery(id+"F8.imprint","IMPRINT",EDGE,{"disambiguationData":[TD([[subQ2,-1.0]])],"derivedFrom":subQ1}),1.0]])]});}
            extrude(context, id + "F9", {"entities" : qUnion([Q0, Q1, Q2, Q3, Q4, Q5, Q6, Q7, Q8, Q9, Q10, Q11, Q12, Q13, Q14, Q15, Q16, Q17, Q18, Q19, Q20, Q21, Q22, Q23, Q24, Q25, Q26, Q27, Q28, Q29]), "operationType" : NewBodyOperationType.REMOVE, "oppositeDirection" : true, "depth" : 1 * mm, "offsetDistance" : 25 * mm});
        }
        {
            var Q0;
            {var subQ0=sQuery(id+"F8.wireOp",EDGE,"E39.0");Q0=makeQuery(id+"F9.boolean.opBoolean","COPY",EDGE,{"derivedFrom":makeQuery(id+"F9.opExtrude","CAP_EDGE",EDGE,{"disambiguationData":[OSD([subQ0]),TDD([makeQuery(id+"F8.imprint","IMPRINT",EDGE,{"disambiguationData":[TD([[makeQuery(id+"F8.imprint","INTERSECT",VERTEX,{"derivedFrom":[subQ0,sQuery(id+"F8.wireOp",EDGE,"E82.0")]}),-1.0]])],"derivedFrom":subQ0})])],"isStart":false})});}
            var Q1;
            {var subQ0=sQuery(id+"F8.wireOp",EDGE,"E39.0");Q1=makeQuery(id+"F9.boolean.opBoolean","COPY",EDGE,{"derivedFrom":makeQuery(id+"F9.opExtrude","CAP_EDGE",EDGE,{"disambiguationData":[OSD([subQ0]),TDD([makeQuery(id+"F8.imprint","IMPRINT",EDGE,{"disambiguationData":[TD([[makeQuery(id+"F8.imprint","INTERSECT",VERTEX,{"derivedFrom":[subQ0,sQuery(id+"F8.wireOp",EDGE,"E84.0")]}),-1.0]])],"derivedFrom":subQ0})])],"isStart":false})});}
            var Q2;
            {var subQ0=sQuery(id+"F8.wireOp",EDGE,"E39.0");Q2=makeQuery(id+"F9.boolean.opBoolean","COPY",EDGE,{"derivedFrom":makeQuery(id+"F9.opExtrude","CAP_EDGE",EDGE,{"disambiguationData":[OSD([subQ0]),TDD([makeQuery(id+"F8.imprint","IMPRINT",EDGE,{"disambiguationData":[TD([[makeQuery(id+"F8.imprint","INTERSECT",VERTEX,{"derivedFrom":[subQ0,sQuery(id+"F8.wireOp",EDGE,"E86.0")]}),-1.0]])],"derivedFrom":subQ0})])],"isStart":false})});}
            var Q3;
            {var subQ0=sQuery(id+"F8.wireOp",EDGE,"E39.0");Q3=makeQuery(id+"F9.boolean.opBoolean","COPY",EDGE,{"derivedFrom":makeQuery(id+"F9.opExtrude","CAP_EDGE",EDGE,{"disambiguationData":[OSD([subQ0]),TDD([makeQuery(id+"F8.imprint","IMPRINT",EDGE,{"disambiguationData":[TD([[makeQuery(id+"F8.imprint","INTERSECT",VERTEX,{"derivedFrom":[subQ0,sQuery(id+"F8.wireOp",EDGE,"E88.0")]}),-1.0]])],"derivedFrom":subQ0})])],"isStart":false})});}
            var Q4;
            {var subQ0=sQuery(id+"F8.wireOp",EDGE,"E39.0");Q4=makeQuery(id+"F9.boolean.opBoolean","COPY",EDGE,{"derivedFrom":makeQuery(id+"F9.opExtrude","CAP_EDGE",EDGE,{"disambiguationData":[OSD([subQ0]),TDD([makeQuery(id+"F8.imprint","IMPRINT",EDGE,{"disambiguationData":[TD([[makeQuery(id+"F8.imprint","INTERSECT",VERTEX,{"derivedFrom":[subQ0,sQuery(id+"F8.wireOp",EDGE,"E90.0")]}),-1.0]])],"derivedFrom":subQ0})])],"isStart":false})});}
            var Q5;
            {var subQ0=sQuery(id+"F8.wireOp",EDGE,"E39.0");Q5=makeQuery(id+"F9.boolean.opBoolean","COPY",EDGE,{"derivedFrom":makeQuery(id+"F9.opExtrude","CAP_EDGE",EDGE,{"disambiguationData":[OSD([subQ0]),TDD([makeQuery(id+"F8.imprint","IMPRINT",EDGE,{"disambiguationData":[TD([[makeQuery(id+"F8.imprint","INTERSECT",VERTEX,{"derivedFrom":[subQ0,sQuery(id+"F8.wireOp",EDGE,"E92.0")]}),-1.0]])],"derivedFrom":subQ0})])],"isStart":false})});}
            var Q6;
            {var subQ0=sQuery(id+"F8.wireOp",EDGE,"E39.0");Q6=makeQuery(id+"F9.boolean.opBoolean","COPY",EDGE,{"derivedFrom":makeQuery(id+"F9.opExtrude","CAP_EDGE",EDGE,{"disambiguationData":[OSD([subQ0]),TDD([makeQuery(id+"F8.imprint","IMPRINT",EDGE,{"disambiguationData":[TD([[makeQuery(id+"F8.imprint","INTERSECT",VERTEX,{"derivedFrom":[subQ0,sQuery(id+"F8.wireOp",EDGE,"E95.0")]}),1.0]])],"derivedFrom":subQ0})])],"isStart":false})});}
            var Q7;
            {var subQ0=sQuery(id+"F8.wireOp",EDGE,"E39.0");Q7=makeQuery(id+"F9.boolean.opBoolean","COPY",EDGE,{"derivedFrom":makeQuery(id+"F9.opExtrude","CAP_EDGE",EDGE,{"disambiguationData":[OSD([subQ0]),TDD([makeQuery(id+"F8.imprint","IMPRINT",EDGE,{"disambiguationData":[TD([[makeQuery(id+"F8.imprint","INTERSECT",VERTEX,{"derivedFrom":[subQ0,sQuery(id+"F8.wireOp",EDGE,"E96.0")]}),-1.0]])],"derivedFrom":subQ0})])],"isStart":false})});}
            var Q8;
            {var subQ0=sQuery(id+"F8.wireOp",EDGE,"E39.0");Q8=makeQuery(id+"F9.boolean.opBoolean","COPY",EDGE,{"derivedFrom":makeQuery(id+"F9.opExtrude","CAP_EDGE",EDGE,{"disambiguationData":[OSD([subQ0]),TDD([makeQuery(id+"F8.imprint","IMPRINT",EDGE,{"disambiguationData":[TD([[makeQuery(id+"F8.imprint","INTERSECT",VERTEX,{"derivedFrom":[subQ0,sQuery(id+"F8.wireOp",EDGE,"E98.0")]}),-1.0]])],"derivedFrom":subQ0})])],"isStart":false})});}
            var Q9;
            {var subQ0=sQuery(id+"F8.wireOp",EDGE,"E39.0");Q9=makeQuery(id+"F9.boolean.opBoolean","COPY",EDGE,{"derivedFrom":makeQuery(id+"F9.opExtrude","CAP_EDGE",EDGE,{"disambiguationData":[OSD([subQ0]),TDD([makeQuery(id+"F8.imprint","IMPRINT",EDGE,{"disambiguationData":[TD([[makeQuery(id+"F8.imprint","INTERSECT",VERTEX,{"derivedFrom":[subQ0,sQuery(id+"F8.wireOp",EDGE,"E40.0")]}),-1.0]])],"derivedFrom":subQ0})])],"isStart":false})});}
            var Q10;
            {var subQ0=sQuery(id+"F8.wireOp",EDGE,"E39.0");Q10=makeQuery(id+"F9.boolean.opBoolean","COPY",EDGE,{"derivedFrom":makeQuery(id+"F9.opExtrude","CAP_EDGE",EDGE,{"disambiguationData":[OSD([subQ0]),TDD([makeQuery(id+"F8.imprint","IMPRINT",EDGE,{"disambiguationData":[TD([[makeQuery(id+"F8.imprint","INTERSECT",VERTEX,{"derivedFrom":[subQ0,sQuery(id+"F8.wireOp",EDGE,"E42.0")]}),-1.0]])],"derivedFrom":subQ0})])],"isStart":false})});}
            var Q11;
            {var subQ0=sQuery(id+"F8.wireOp",EDGE,"E39.0");Q11=makeQuery(id+"F9.boolean.opBoolean","COPY",EDGE,{"derivedFrom":makeQuery(id+"F9.opExtrude","CAP_EDGE",EDGE,{"disambiguationData":[OSD([subQ0]),TDD([makeQuery(id+"F8.imprint","IMPRINT",EDGE,{"disambiguationData":[TD([[makeQuery(id+"F8.imprint","INTERSECT",VERTEX,{"derivedFrom":[subQ0,sQuery(id+"F8.wireOp",EDGE,"E44.0")]}),-1.0]])],"derivedFrom":subQ0})])],"isStart":false})});}
            var Q12;
            {var subQ0=sQuery(id+"F8.wireOp",EDGE,"E39.0");Q12=makeQuery(id+"F9.boolean.opBoolean","COPY",EDGE,{"derivedFrom":makeQuery(id+"F9.opExtrude","CAP_EDGE",EDGE,{"disambiguationData":[OSD([subQ0]),TDD([makeQuery(id+"F8.imprint","IMPRINT",EDGE,{"disambiguationData":[TD([[makeQuery(id+"F8.imprint","INTERSECT",VERTEX,{"derivedFrom":[subQ0,sQuery(id+"F8.wireOp",EDGE,"E46.0")]}),-1.0]])],"derivedFrom":subQ0})])],"isStart":false})});}
            var Q13;
            {var subQ0=sQuery(id+"F8.wireOp",EDGE,"E39.0");Q13=makeQuery(id+"F9.boolean.opBoolean","COPY",EDGE,{"derivedFrom":makeQuery(id+"F9.opExtrude","CAP_EDGE",EDGE,{"disambiguationData":[OSD([subQ0]),TDD([makeQuery(id+"F8.imprint","IMPRINT",EDGE,{"disambiguationData":[TD([[makeQuery(id+"F8.imprint","INTERSECT",VERTEX,{"derivedFrom":[subQ0,sQuery(id+"F8.wireOp",EDGE,"E48.0")]}),-1.0]])],"derivedFrom":subQ0})])],"isStart":false})});}
            var Q14;
            {var subQ0=sQuery(id+"F8.wireOp",EDGE,"E39.0");Q14=makeQuery(id+"F9.boolean.opBoolean","COPY",EDGE,{"derivedFrom":makeQuery(id+"F9.opExtrude","CAP_EDGE",EDGE,{"disambiguationData":[OSD([subQ0]),TDD([makeQuery(id+"F8.imprint","IMPRINT",EDGE,{"disambiguationData":[TD([[makeQuery(id+"F8.imprint","INTERSECT",VERTEX,{"derivedFrom":[subQ0,sQuery(id+"F8.wireOp",EDGE,"E50.0")]}),-1.0]])],"derivedFrom":subQ0})])],"isStart":false})});}
            var Q15;
            {var subQ0=sQuery(id+"F8.wireOp",EDGE,"E39.0");Q15=makeQuery(id+"F9.boolean.opBoolean","COPY",EDGE,{"derivedFrom":makeQuery(id+"F9.opExtrude","CAP_EDGE",EDGE,{"disambiguationData":[OSD([subQ0]),TDD([makeQuery(id+"F8.imprint","IMPRINT",EDGE,{"disambiguationData":[TD([[makeQuery(id+"F8.imprint","INTERSECT",VERTEX,{"derivedFrom":[subQ0,sQuery(id+"F8.wireOp",EDGE,"E52.0")]}),-1.0]])],"derivedFrom":subQ0})])],"isStart":false})});}
            var Q16;
            {var subQ0=sQuery(id+"F8.wireOp",EDGE,"E39.0");Q16=makeQuery(id+"F9.boolean.opBoolean","COPY",EDGE,{"derivedFrom":makeQuery(id+"F9.opExtrude","CAP_EDGE",EDGE,{"disambiguationData":[OSD([subQ0]),TDD([makeQuery(id+"F8.imprint","IMPRINT",EDGE,{"disambiguationData":[TD([[makeQuery(id+"F8.imprint","INTERSECT",VERTEX,{"derivedFrom":[subQ0,sQuery(id+"F8.wireOp",EDGE,"E54.0")]}),-1.0]])],"derivedFrom":subQ0})])],"isStart":false})});}
            var Q17;
            {var subQ0=sQuery(id+"F8.wireOp",EDGE,"E39.0");Q17=makeQuery(id+"F9.boolean.opBoolean","COPY",EDGE,{"derivedFrom":makeQuery(id+"F9.opExtrude","CAP_EDGE",EDGE,{"disambiguationData":[OSD([subQ0]),TDD([makeQuery(id+"F8.imprint","IMPRINT",EDGE,{"disambiguationData":[TD([[makeQuery(id+"F8.imprint","INTERSECT",VERTEX,{"derivedFrom":[subQ0,sQuery(id+"F8.wireOp",EDGE,"E56.0")]}),-1.0]])],"derivedFrom":subQ0})])],"isStart":false})});}
            var Q18;
            {var subQ0=sQuery(id+"F8.wireOp",EDGE,"E39.0");Q18=makeQuery(id+"F9.boolean.opBoolean","COPY",EDGE,{"derivedFrom":makeQuery(id+"F9.opExtrude","CAP_EDGE",EDGE,{"disambiguationData":[OSD([subQ0]),TDD([makeQuery(id+"F8.imprint","IMPRINT",EDGE,{"disambiguationData":[TD([[makeQuery(id+"F8.imprint","INTERSECT",VERTEX,{"derivedFrom":[subQ0,sQuery(id+"F8.wireOp",EDGE,"E58.0")]}),-1.0]])],"derivedFrom":subQ0})])],"isStart":false})});}
            var Q19;
            {var subQ0=sQuery(id+"F8.wireOp",EDGE,"E39.0");Q19=makeQuery(id+"F9.boolean.opBoolean","COPY",EDGE,{"derivedFrom":makeQuery(id+"F9.opExtrude","CAP_EDGE",EDGE,{"disambiguationData":[OSD([subQ0]),TDD([makeQuery(id+"F8.imprint","IMPRINT",EDGE,{"disambiguationData":[TD([[makeQuery(id+"F8.imprint","INTERSECT",VERTEX,{"derivedFrom":[subQ0,sQuery(id+"F8.wireOp",EDGE,"E60.0")]}),-1.0]])],"derivedFrom":subQ0})])],"isStart":false})});}
            var Q20;
            {var subQ0=sQuery(id+"F8.wireOp",EDGE,"E39.0");Q20=makeQuery(id+"F9.boolean.opBoolean","COPY",EDGE,{"derivedFrom":makeQuery(id+"F9.opExtrude","CAP_EDGE",EDGE,{"disambiguationData":[OSD([subQ0]),TDD([makeQuery(id+"F8.imprint","IMPRINT",EDGE,{"disambiguationData":[TD([[makeQuery(id+"F8.imprint","INTERSECT",VERTEX,{"derivedFrom":[subQ0,sQuery(id+"F8.wireOp",EDGE,"E62.0")]}),-1.0]])],"derivedFrom":subQ0})])],"isStart":false})});}
            var Q21;
            {var subQ0=sQuery(id+"F8.wireOp",EDGE,"E39.0");Q21=makeQuery(id+"F9.boolean.opBoolean","COPY",EDGE,{"derivedFrom":makeQuery(id+"F9.opExtrude","CAP_EDGE",EDGE,{"disambiguationData":[OSD([subQ0]),TDD([makeQuery(id+"F8.imprint","IMPRINT",EDGE,{"disambiguationData":[TD([[makeQuery(id+"F8.imprint","INTERSECT",VERTEX,{"derivedFrom":[subQ0,sQuery(id+"F8.wireOp",EDGE,"E64.0")]}),-1.0]])],"derivedFrom":subQ0})])],"isStart":false})});}
            var Q22;
            {var subQ0=sQuery(id+"F8.wireOp",EDGE,"E39.0");Q22=makeQuery(id+"F9.boolean.opBoolean","COPY",EDGE,{"derivedFrom":makeQuery(id+"F9.opExtrude","CAP_EDGE",EDGE,{"disambiguationData":[OSD([subQ0]),TDD([makeQuery(id+"F8.imprint","IMPRINT",EDGE,{"disambiguationData":[TD([[makeQuery(id+"F8.imprint","INTERSECT",VERTEX,{"derivedFrom":[subQ0,sQuery(id+"F8.wireOp",EDGE,"E66.0")]}),-1.0]])],"derivedFrom":subQ0})])],"isStart":false})});}
            var Q23;
            {var subQ0=sQuery(id+"F8.wireOp",EDGE,"E39.0");Q23=makeQuery(id+"F9.boolean.opBoolean","COPY",EDGE,{"derivedFrom":makeQuery(id+"F9.opExtrude","CAP_EDGE",EDGE,{"disambiguationData":[OSD([subQ0]),TDD([makeQuery(id+"F8.imprint","IMPRINT",EDGE,{"disambiguationData":[TD([[makeQuery(id+"F8.imprint","INTERSECT",VERTEX,{"derivedFrom":[subQ0,sQuery(id+"F8.wireOp",EDGE,"E68.0")]}),-1.0]])],"derivedFrom":subQ0})])],"isStart":false})});}
            var Q24;
            {var subQ0=sQuery(id+"F8.wireOp",EDGE,"E39.0");Q24=makeQuery(id+"F9.boolean.opBoolean","COPY",EDGE,{"derivedFrom":makeQuery(id+"F9.opExtrude","CAP_EDGE",EDGE,{"disambiguationData":[OSD([subQ0]),TDD([makeQuery(id+"F8.imprint","IMPRINT",EDGE,{"disambiguationData":[TD([[makeQuery(id+"F8.imprint","INTERSECT",VERTEX,{"derivedFrom":[subQ0,sQuery(id+"F8.wireOp",EDGE,"E70.0")]}),-1.0]])],"derivedFrom":subQ0})])],"isStart":false})});}
            var Q25;
            {var subQ0=sQuery(id+"F8.wireOp",EDGE,"E39.0");Q25=makeQuery(id+"F9.boolean.opBoolean","COPY",EDGE,{"derivedFrom":makeQuery(id+"F9.opExtrude","CAP_EDGE",EDGE,{"disambiguationData":[OSD([subQ0]),TDD([makeQuery(id+"F8.imprint","IMPRINT",EDGE,{"disambiguationData":[TD([[makeQuery(id+"F8.imprint","INTERSECT",VERTEX,{"derivedFrom":[subQ0,sQuery(id+"F8.wireOp",EDGE,"E80.0")]}),-1.0]])],"derivedFrom":subQ0})])],"isStart":false})});}
            var Q26;
            {var subQ0=sQuery(id+"F8.wireOp",EDGE,"E39.0");Q26=makeQuery(id+"F9.boolean.opBoolean","COPY",EDGE,{"derivedFrom":makeQuery(id+"F9.opExtrude","CAP_EDGE",EDGE,{"disambiguationData":[OSD([subQ0]),TDD([makeQuery(id+"F8.imprint","IMPRINT",EDGE,{"disambiguationData":[TD([[makeQuery(id+"F8.imprint","INTERSECT",VERTEX,{"derivedFrom":[subQ0,sQuery(id+"F8.wireOp",EDGE,"E78.0")]}),-1.0]])],"derivedFrom":subQ0})])],"isStart":false})});}
            var Q27;
            {var subQ0=sQuery(id+"F8.wireOp",EDGE,"E39.0");Q27=makeQuery(id+"F9.boolean.opBoolean","COPY",EDGE,{"derivedFrom":makeQuery(id+"F9.opExtrude","CAP_EDGE",EDGE,{"disambiguationData":[OSD([subQ0]),TDD([makeQuery(id+"F8.imprint","IMPRINT",EDGE,{"disambiguationData":[TD([[makeQuery(id+"F8.imprint","INTERSECT",VERTEX,{"derivedFrom":[subQ0,sQuery(id+"F8.wireOp",EDGE,"E76.0")]}),-1.0]])],"derivedFrom":subQ0})])],"isStart":false})});}
            var Q28;
            {var subQ0=sQuery(id+"F8.wireOp",EDGE,"E39.0");Q28=makeQuery(id+"F9.boolean.opBoolean","COPY",EDGE,{"derivedFrom":makeQuery(id+"F9.opExtrude","CAP_EDGE",EDGE,{"disambiguationData":[OSD([subQ0]),TDD([makeQuery(id+"F8.imprint","IMPRINT",EDGE,{"disambiguationData":[TD([[makeQuery(id+"F8.imprint","INTERSECT",VERTEX,{"derivedFrom":[subQ0,sQuery(id+"F8.wireOp",EDGE,"E74.0")]}),-1.0]])],"derivedFrom":subQ0})])],"isStart":false})});}
            var Q29;
            {var subQ0=sQuery(id+"F8.wireOp",EDGE,"E39.0");Q29=makeQuery(id+"F9.boolean.opBoolean","COPY",EDGE,{"derivedFrom":makeQuery(id+"F9.opExtrude","CAP_EDGE",EDGE,{"disambiguationData":[OSD([subQ0]),TDD([makeQuery(id+"F8.imprint","IMPRINT",EDGE,{"disambiguationData":[TD([[makeQuery(id+"F8.imprint","INTERSECT",VERTEX,{"derivedFrom":[subQ0,sQuery(id+"F8.wireOp",EDGE,"E72.0")]}),-1.0]])],"derivedFrom":subQ0})])],"isStart":false})});}
            chamfer(context, id + "F10", {"entities" : qUnion([Q0, Q1, Q2, Q3, Q4, Q5, Q6, Q7, Q8, Q9, Q10, Q11, Q12, Q13, Q14, Q15, Q16, Q17, Q18, Q19, Q20, Q21, Q22, Q23, Q24, Q25, Q26, Q27, Q28, Q29]), "width" : 0.8 * mm, "tangentPropagation" : true});
        }
        {
            var Q0;
            Q0=makeQuery(id+"F1.opRevolve","SWEPT_FACE",FACE,{"disambiguationData":[OSD([sQuery(id+"F0.wireOp",EDGE,"E5.top"),sQuery(id+"F0.wireOp",EDGE,"E7.bottom")])]});
            extrude(context, id + "F11", {"entities" : qUnion([Q0]), "operationType" : NewBodyOperationType.REMOVE, "oppositeDirection" : true, "depth" : 14 * mm, "offsetDistance" : 25 * mm});
        }
    });
